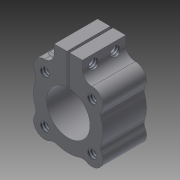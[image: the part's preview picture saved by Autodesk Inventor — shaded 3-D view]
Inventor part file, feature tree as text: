
AUTODESK INVENTOR PART (.ipt)
format: ipt  version: 2015 (Build 190159000, 159)  size: 268,288 bytes
history: native  units: in
note: dims shown in document units (in); Inventor stores cm internally (conversion verified against a paired STEP export)
features: hole x35, sketch x18, thread x12, other x1, extrude x1, imported_body x1
ambient origin geometry x8: Origin, YZ Plane, XZ Plane, XY Plane, X Axis, Y Axis, Z Axis, Center Point
bodies: Solid1 (feature_tree)
feature tree (68):
  other  "User Library-545340.sat1"
  thread  "Thread1"  [1 undecoded]
  thread  "Thread2"  [1 undecoded]
  thread  "Thread3"  [1 undecoded]
  thread  "Thread4"  [1 undecoded]
  thread  "Thread5"  [1 undecoded]
  thread  "Thread6"  [1 undecoded]
  thread  "Thread7"  [1 undecoded]
  thread  "Thread8"  [1 undecoded]
  hole  "Hole1"  [1 undecoded]
  hole  "Hole4"  [1 undecoded]
  hole  "Hole6"  [1 undecoded]
  hole  "Hole8"  [1 undecoded]
  hole  "Hole10"  [1 undecoded]
  hole  "Hole12"  [1 undecoded]
  hole  "Hole14"  [1 undecoded]
  hole  "Hole16"  [1 undecoded]
  hole  "Hole18"  [1 undecoded]
  thread  "Thread9"  [1 undecoded]
  thread  "Thread10"  [1 undecoded]
  thread  "Thread11"  [1 undecoded]
  thread  "Thread12"  [1 undecoded]
  hole  "Hole20"  [1 undecoded]
  hole  "Hole22"  [1 undecoded]
  hole  "Hole24"  [1 undecoded]
  hole  "Hole26"  [1 undecoded]
  sketch  "Sketch16"  dims[d108=0.104in d109=0.2565in d110=0.375in d111=0.25in d112=0.5635in d113=0.3255in d114=120.0deg]
  extrude  "Extrusion1"  [1 undecoded]
  hole  "Hole27"  [1 undecoded]
  hole  "Hole29"  [1 undecoded]
  hole  "Hole31"  [1 undecoded]
  hole  "Hole33"  [1 undecoded]
  hole  "Hole35"  [1 undecoded]
  imported_body  "Base1"
  sketch  "Sketch3"  dims[d23=0.104in d24=0.339in d25=0.375in d26=0.25in d27=0.5635in d28=0.408in d29=120.0deg]
  hole  "Hole2"  [1 undecoded]
  sketch  "Sketch4"  dims[d30=0.104in d31=0.2706in d32=0.375in d33=0.25in d34=0.5635in d35=0.3396in d36=120.0deg]
  hole  "Hole3"  [1 undecoded]
  sketch  "Sketch5"  dims[d37=0.104in d38=0.339in d39=0.375in d40=0.25in d41=0.5635in d42=0.408in d43=120.0deg]
  hole  "Hole5"  [1 undecoded]
  sketch  "Sketch6"  dims[d44=0.104in d45=0.138in d46=0.375in d47=0.25in d48=0.5635in d49=0.207in d50=120.0deg]
  hole  "Hole7"  [1 undecoded]
  sketch  "Sketch7"  dims[d51=0.104in d52=0.339in d53=0.375in d54=0.25in d55=0.5635in d56=0.408in d57=120.0deg]
  hole  "Hole9"  [1 undecoded]
  sketch  "Sketch8"  dims[d58=0.104in d59=0.339in d60=0.375in d61=0.25in d62=0.5635in d63=0.408in d64=120.0deg]
  hole  "Hole11"  [1 undecoded]
  sketch  "Sketch9"  dims[d65=0.104in d66=0.339in d67=0.375in d68=0.25in d69=0.5635in d70=0.408in d71=120.0deg]
  hole  "Hole13"  [1 undecoded]
  sketch  "Sketch10"  dims[d72=0.104in d73=0.339in d74=0.375in d75=0.25in d76=0.5635in d77=0.408in d78=120.0deg]
  hole  "Hole15"  [1 undecoded]
  sketch  "Sketch11"  dims[d79=0.104in d80=0.339in d81=0.375in d82=0.25in d83=0.5635in d84=0.408in d85=120.0deg d86=1.0in d87=0.0in]
  hole  "Hole17"  [1 undecoded]
  sketch  "Sketch12"  dims[d88=1.0in d89=0.0in d90=1.0in d91=0.0in]
  hole  "Hole19"  [1 undecoded]
  sketch  "Sketch13"  dims[d92=1.0in d93=0.0in]
  hole  "Hole21"  [1 undecoded]
  sketch  "Sketch14"  dims[d94=0.104in d95=0.2565in d96=0.375in d97=0.25in d98=0.5635in d99=0.3255in d100=120.0deg]
  hole  "Hole23"  [1 undecoded]
  sketch  "Sketch15"  dims[d101=0.104in d102=0.2565in d103=0.375in d104=0.25in d105=0.5635in d106=0.3255in d107=120.0deg]
  hole  "Hole25"  [1 undecoded]
  sketch  "Sketch17"  dims[d115=0.104in d116=0.2565in d117=0.375in d118=0.25in d119=0.5635in d120=0.3255in d121=120.0deg d122=1.0in d123=0.0in]
  hole  "Hole28"  [1 undecoded]
  sketch  "Sketch18"  dims[d124=0.14in d125=0.75in d126=0.375in d127=0.25in d128=0.5635in d129=1.0in d130=0.0in]
  hole  "Hole30"  [1 undecoded]
  sketch  "Sketch19"  dims[d131=0.104in d132=0.2042in d133=0.375in d134=0.25in d135=0.5635in d136=0.2732in d137=120.0deg]
  hole  "Hole32"  [1 undecoded]
  sketch  "Sketch20"  dims[d138=0.104in d139=0.2042in d140=0.375in d141=0.25in d142=0.5635in d143=0.2732in d144=120.0deg d145=0.104in d146=0.2042in d147=0.375in d148=0.25in d149=0.5635in d150=0.2732in d151=120.0deg d152=0.104in d153=0.2042in d154=0.375in d155=0.25in d156=0.5635in d157=0.2732in d158=120.0deg]
  hole  "Hole34"  [1 undecoded]
note: 48 required parameter values undecoded (feature->parameter linkage not recoverable at this tier; creation-order binding heuristic only, values carry confidence <= 0.55)
